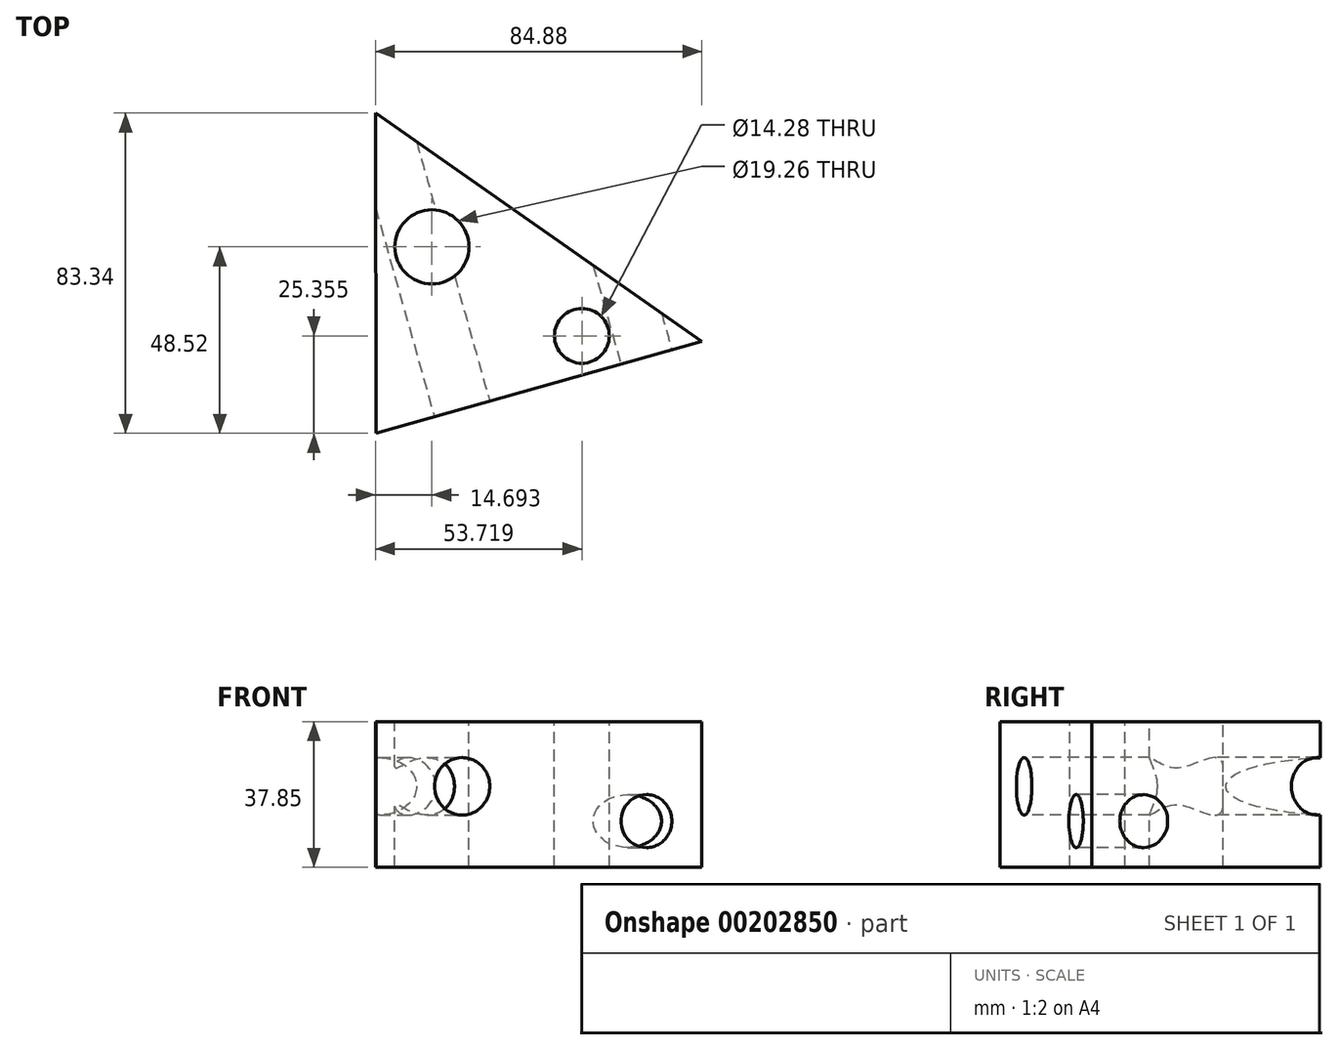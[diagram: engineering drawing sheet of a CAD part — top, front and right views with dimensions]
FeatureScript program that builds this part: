
annotation { "Feature Type Name" : "Feature", "Feature Type Description" : "" }
export const myFeature = defineFeature(function(context is Context, id is Id, definition is map)
    precondition{}
    {
        {
            var Q0;
            Q0=qCreatedBy(makeId("Top.planeOp"),FACE);
            var sketch = newSketch(context, id + "F0", { "sketchPlane" : qUnion([Q0])});
            skLineSegment(sketch, "E0", {"start": v(-66.88, -48.52) * mm, "end": v(-67.02, 34.82) * mm});
            skLineSegment(sketch, "E1", {"start": v(-67.02, 34.82) * mm, "end": v(17.86, -24.62) * mm});
            skLineSegment(sketch, "E2", {"start": v(17.86, -24.62) * mm, "end": v(-66.88, -48.52) * mm});
            skSolve(sketch);
        }
        {
            var Q0;
            Q0 = qSketchRegion(id + "F0", true);
            extrude(context, id + "F1", {"entities" : qUnion([Q0]), "depth" : 37.85 * mm});
        }
        {
            var Q0;
            Q0=makeQuery(id+"F1.opExtrude","SWEPT_FACE",FACE,{"disambiguationData":[OSD([sQuery(id+"F0.wireOp",EDGE,"E2")])]});
            var sketch = newSketch(context, id + "F2", { "sketchPlane" : qUnion([Q0])});
            skCircle(sketch, "E3", {"center": v(-54.24, 21.04) * mm, "radius": 7.47 * mm});
            skSolve(sketch);
        }
        {
            var Q0;
            Q0 = qSketchRegion(id + "F2", true);
            extrude(context, id + "F3", {"entities" : qUnion([Q0]), "operationType" : NewBodyOperationType.REMOVE, "endBound" : BoundingType.THROUGH_ALL, "oppositeDirection" : true, "depth" : 25.4 * mm});
        }
        {
            var Q0;
            Q0=makeQuery(id+"F1.opExtrude","CAP_FACE",FACE,{"disambiguationData":[OSD([sQuery(id+"F0.wireOp",EDGE,"E0"),sQuery(id+"F0.wireOp",EDGE,"E1"),sQuery(id+"F0.wireOp",EDGE,"E2")])],"isStart":false});
            var sketch = newSketch(context, id + "F4", { "sketchPlane" : qUnion([Q0])});
            skCircle(sketch, "E4", {"center": v(-13.3, -23.17) * mm, "radius": 7.14 * mm});
            skSolve(sketch);
        }
        {
            var Q0;
            Q0 = qSketchRegion(id + "F4", true);
            extrude(context, id + "F5", {"entities" : qUnion([Q0]), "operationType" : NewBodyOperationType.REMOVE, "endBound" : BoundingType.THROUGH_ALL, "oppositeDirection" : true, "depth" : 25.4 * mm});
        }
        {
            var Q0;
            Q0=makeQuery(id+"F1.opExtrude","SWEPT_FACE",FACE,{"disambiguationData":[OSD([sQuery(id+"F0.wireOp",EDGE,"E2")])]});
            var sketch = newSketch(context, id + "F6", { "sketchPlane" : qUnion([Q0])});
            skCircle(sketch, "E5", {"center": v(-4.44, 11.99) * mm, "radius": 6.88 * mm});
            skSolve(sketch);
        }
        {
            var Q0;
            Q0 = qSketchRegion(id + "F6", true);
            extrude(context, id + "F7", {"entities" : qUnion([Q0]), "operationType" : NewBodyOperationType.REMOVE, "endBound" : BoundingType.THROUGH_ALL, "oppositeDirection" : true, "depth" : 25.4 * mm});
        }
        {
            var Q0;
            Q0=makeQuery(id+"F1.opExtrude","CAP_FACE",FACE,{"disambiguationData":[OSD([sQuery(id+"F0.wireOp",EDGE,"E0"),sQuery(id+"F0.wireOp",EDGE,"E1"),sQuery(id+"F0.wireOp",EDGE,"E2")])],"isStart":false});
            var sketch = newSketch(context, id + "F8", { "sketchPlane" : qUnion([Q0])});
            skCircle(sketch, "E6", {"center": v(-52.33, 0) * mm, "radius": 9.63 * mm});
            skSolve(sketch);
        }
        {
            var Q0;
            Q0=makeQuery(id+"F8.imprint","IMPRINT",FACE,{"disambiguationData":[TD([[makeQuery(id+"F8.imprint","IMPRINT",EDGE,{"derivedFrom":sQuery(id+"F8.wireOp",EDGE,"E6")}),1.0]])]});
            extrude(context, id + "F9", {"entities" : qUnion([Q0]), "operationType" : NewBodyOperationType.REMOVE, "endBound" : BoundingType.THROUGH_ALL, "oppositeDirection" : true, "depth" : 25.4 * mm});
        }
    });
